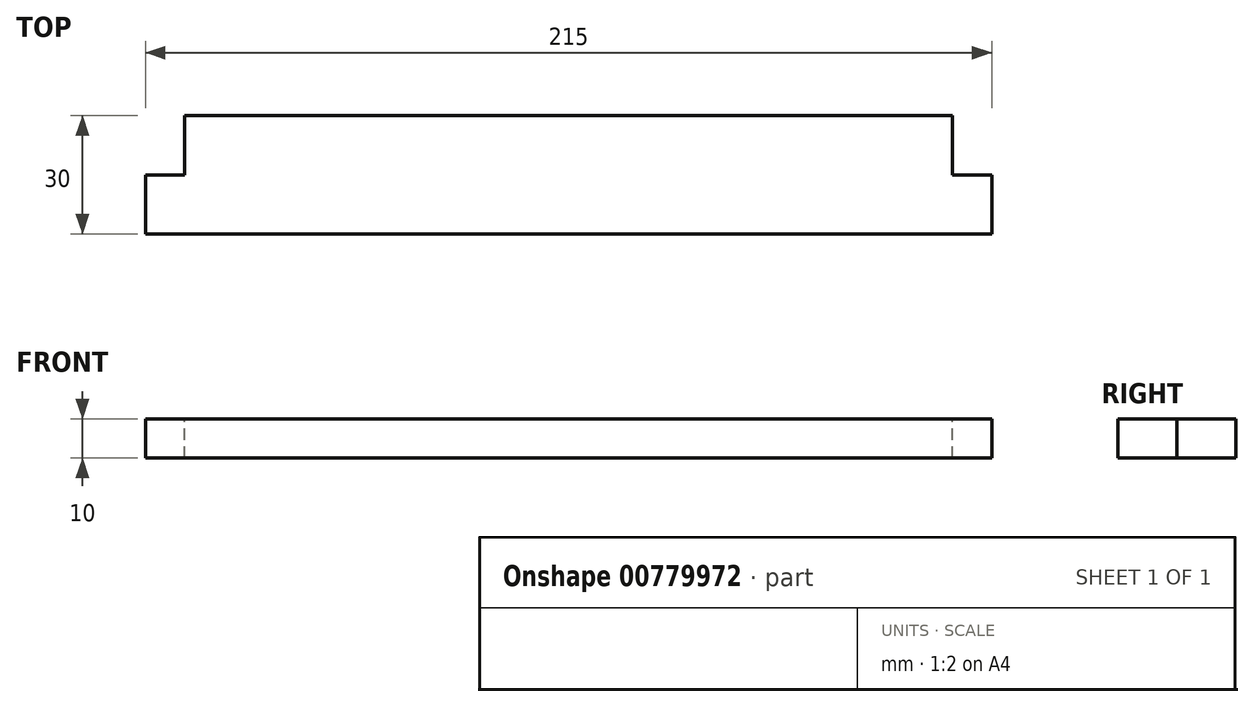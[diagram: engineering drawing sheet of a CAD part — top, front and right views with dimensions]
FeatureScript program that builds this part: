
annotation { "Feature Type Name" : "Feature", "Feature Type Description" : "" }
export const myFeature = defineFeature(function(context is Context, id is Id, definition is map)
    precondition{}
    {
        {
            var Q0;
            Q0=qCreatedBy(makeId("Top.planeOp"),FACE);
            var sketch = newSketch(context, id + "F0", { "sketchPlane" : qUnion([Q0])});
            skLineSegment(sketch, "E0", {"start": v(0, 0) * mm, "end": v(0, 30) * mm});
            skLineSegment(sketch, "E1", {"start": v(0, 30) * mm, "end": v(215, 30) * mm});
            skLineSegment(sketch, "E2", {"start": v(215, 30) * mm, "end": v(215, 0) * mm});
            skLineSegment(sketch, "E3", {"start": v(215, 0) * mm, "end": v(0, 0) * mm});
            skSolve(sketch);
        }
        {
            var Q0;
            Q0 = qSketchRegion(id + "F0", true);
            extrude(context, id + "F1", {"entities" : qUnion([Q0]), "flatOperationType" : FlatOperationType.REMOVE, "depth" : 10 * mm, "offsetDistance" : 25 * mm, "domain" : OperationDomain.MODEL});
        }
        {
            var Q0;
            Q0=makeQuery(id+"F1.opExtrude","CAP_FACE",FACE,{"disambiguationData":[OSD([sQuery(id+"F0.wireOp",EDGE,"E0"),sQuery(id+"F0.wireOp",EDGE,"E1"),sQuery(id+"F0.wireOp",EDGE,"E2"),sQuery(id+"F0.wireOp",EDGE,"E3")])],"isStart":false});
            var sketch = newSketch(context, id + "F2", { "sketchPlane" : qUnion([Q0])});
            skLineSegment(sketch, "E4", {"start": v(0, 30) * mm, "end": v(10, 30) * mm});
            skLineSegment(sketch, "E5", {"start": v(10, 30) * mm, "end": v(10, 15) * mm});
            skLineSegment(sketch, "E6", {"start": v(10, 15) * mm, "end": v(0, 15) * mm});
            skLineSegment(sketch, "E7", {"start": v(215, 30) * mm, "end": v(205, 30) * mm});
            skLineSegment(sketch, "E8", {"start": v(205, 30) * mm, "end": v(205, 15) * mm});
            skLineSegment(sketch, "E9", {"start": v(205, 15) * mm, "end": v(215, 15) * mm});
            skLineSegment(sketch, "E10", {"start": v(0, 15) * mm, "end": v(0, 30) * mm});
            skLineSegment(sketch, "E11", {"start": v(215, 30) * mm, "end": v(215, 15) * mm});
            skSolve(sketch);
        }
        {
            var Q0;
            Q0 = qSketchRegion(id + "F2", true);
            extrude(context, id + "F3", {"entities" : qUnion([Q0]), "operationType" : NewBodyOperationType.REMOVE, "endBound" : BoundingType.THROUGH_ALL, "oppositeDirection" : true, "depth" : 25 * mm, "offsetDistance" : 25 * mm});
        }
    });
